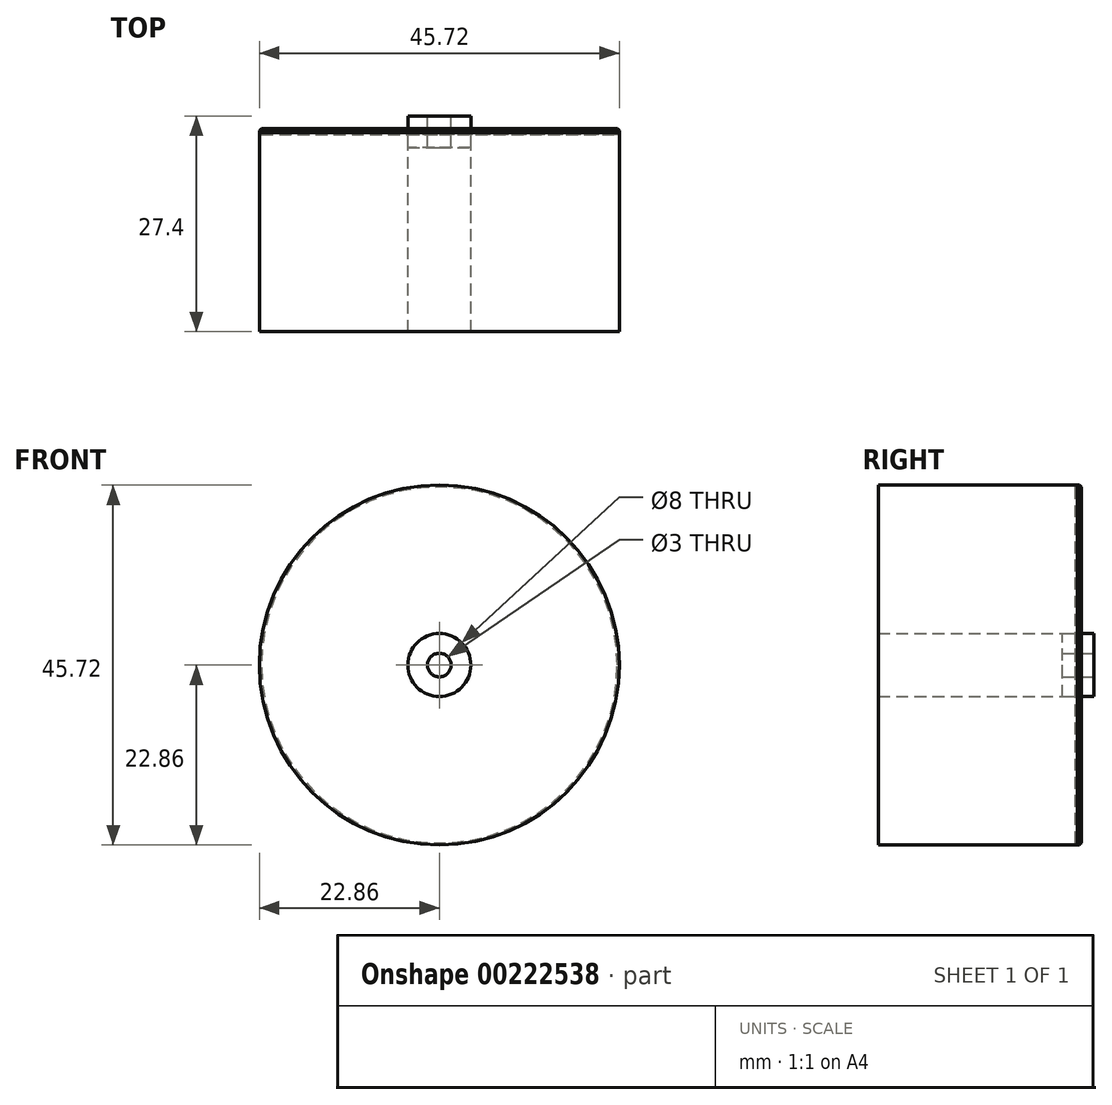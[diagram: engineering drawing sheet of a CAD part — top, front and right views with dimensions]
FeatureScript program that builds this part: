
annotation { "Feature Type Name" : "Feature", "Feature Type Description" : "" }
export const myFeature = defineFeature(function(context is Context, id is Id, definition is map)
    precondition{}
    {
        {
            var Q0;
            Q0=qCreatedBy(makeId("Front.planeOp"),FACE);
            var sketch = newSketch(context, id + "F0", { "sketchPlane" : qUnion([Q0])});
            skCircle(sketch, "E0", {"center": v(0, 0) * mm, "radius": 22.86 * mm});
            skCircle(sketch, "E1", {"center": v(0, 0) * mm, "radius": 4 * mm});
            skSolve(sketch);
        }
        {
            var Q0;
            Q0 = qSketchRegion(id + "F0", true);
            extrude(context, id + "F1", {"entities" : qUnion([Q0]), "endBound" : BoundingType.SYMMETRIC, "depth" : 0.76 * mm});
        }
        {
            var Q0;
            Q0=makeQuery(id+"F1.opExtrude","CAP_EDGE",EDGE,{"disambiguationData":[OSD([sQuery(id+"F0.wireOp",EDGE,"E0")])],"isStart":false});
            var Q1;
            Q1=makeQuery(id+"F1.opExtrude","CAP_EDGE",EDGE,{"disambiguationData":[OSD([sQuery(id+"F0.wireOp",EDGE,"E0")])],"isStart":true});
            chamfer(context, id + "F2", {"entities" : qUnion([Q0, Q1]), "width" : 0.25 * mm, "tangentPropagation" : true});
        }
        {
            var Q0;
            Q0=qCreatedBy(makeId("Front.planeOp"),FACE);
            var sketch = newSketch(context, id + "F3", { "sketchPlane" : qUnion([Q0])});
            skCircle(sketch, "E2", {"center": v(0, 0) * mm, "radius": 4 * mm});
            skCircle(sketch, "E3", {"center": v(0, 0) * mm, "radius": 1.5 * mm});
            skSolve(sketch);
        }
        {
            var Q0;
            Q0=makeQuery(id+"F3.imprint","IMPRINT",FACE,{"disambiguationData":[TD([[makeQuery(id+"F3.imprint","IMPRINT",EDGE,{"derivedFrom":sQuery(id+"F3.wireOp",EDGE,"E2")}),1.0]])]});
            extrude(context, id + "F4", {"entities" : qUnion([Q0]), "operationType" : NewBodyOperationType.ADD, "endBound" : BoundingType.SYMMETRIC, "depth" : 4 * mm});
        }
        {
            var Q0;
            Q0 = qSketchRegion(id + "F0", true);
            extrude(context, id + "F5", {"entities" : qUnion([Q0]), "depth" : 25.4 * mm});
        }
    });
